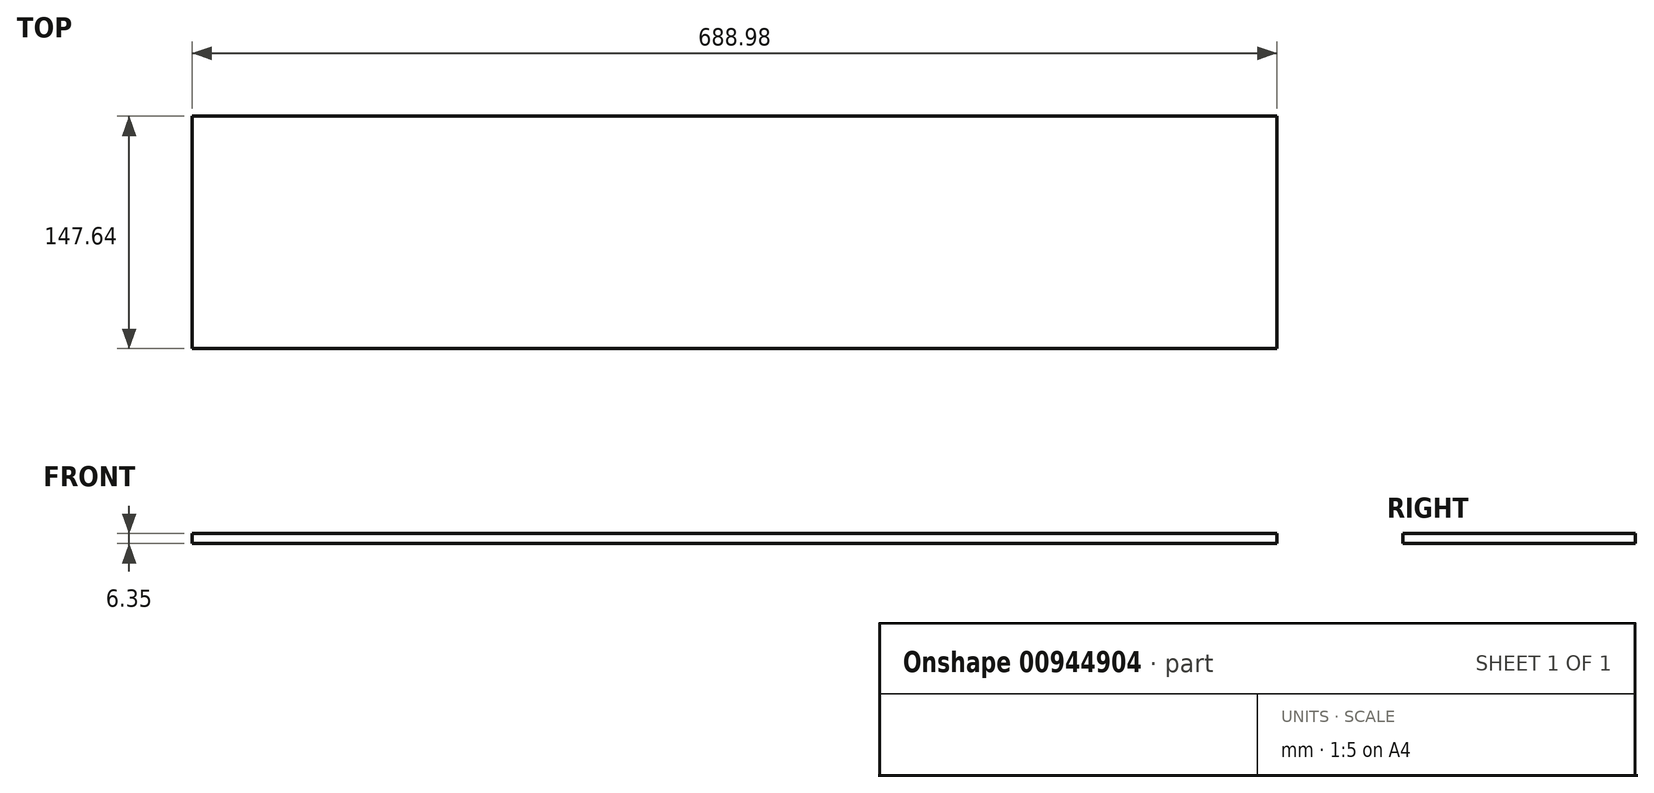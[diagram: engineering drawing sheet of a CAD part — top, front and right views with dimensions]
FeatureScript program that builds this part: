
annotation { "Feature Type Name" : "Feature", "Feature Type Description" : "" }
export const myFeature = defineFeature(function(context is Context, id is Id, definition is map)
    precondition{}
    {
        {
            var Q0;
            Q0=qCreatedBy(makeId("Top.planeOp"),FACE);
            var sketch = newSketch(context, id + "F0", { "sketchPlane" : qUnion([Q0])});
            skLineSegment(sketch, "E0.bottom", {"start": v(-953.72, 1555.2) * mm, "end": v(30.53, 1555.2) * mm});
            skLineSegment(sketch, "E0.top", {"start": v(-953.72, -45) * mm, "end": v(30.53, -45) * mm});
            skLineSegment(sketch, "E0.left", {"start": v(-953.72, 1555.2) * mm, "end": v(-953.72, -45) * mm});
            skLineSegment(sketch, "E0.right", {"start": v(30.53, 1555.2) * mm, "end": v(30.53, -45) * mm});
            skLineSegment(sketch, "E1", {"start": v(-806.08, 1555.2) * mm, "end": v(-806.08, -45) * mm});
            skLineSegment(sketch, "E2", {"start": v(-953.72, 1555.2) * mm, "end": v(-806.08, 1555.2) * mm});
            skLineSegment(sketch, "E3.0", {"start": v(-802.9, 1555.2) * mm, "end": v(-802.9, -45) * mm});
            skLineSegment(sketch, "E4", {"start": v(30.53, 1555.2) * mm, "end": v(-117.1, 1555.2) * mm});
            skLineSegment(sketch, "E5", {"start": v(-117.1, 1555.2) * mm, "end": v(-117.1, -45) * mm});
            skLineSegment(sketch, "E6.0", {"start": v(-120.28, 1555.2) * mm, "end": v(-120.28, -45) * mm});
            skLineSegment(sketch, "E7", {"start": v(-953.72, 1555.2) * mm, "end": v(-953.72, 1407.57) * mm});
            skLineSegment(sketch, "E8", {"start": v(-953.72, 1407.57) * mm, "end": v(30.53, 1407.57) * mm});
            skLineSegment(sketch, "E9.0", {"start": v(-953.72, 1404.4) * mm, "end": v(30.53, 1404.4) * mm});
            skLineSegment(sketch, "E10", {"start": v(-953.72, -45) * mm, "end": v(-953.72, 102.65) * mm});
            skLineSegment(sketch, "E11", {"start": v(-953.72, 102.65) * mm, "end": v(30.53, 102.65) * mm});
            skLineSegment(sketch, "E12.0", {"start": v(-953.72, 105.82) * mm, "end": v(30.53, 105.82) * mm});
            skLineSegment(sketch, "E13.bottom", {"start": v(593.6, 1457) * mm, "end": v(1577.84, 1457) * mm});
            skLineSegment(sketch, "E13.top", {"start": v(593.6, -143.2) * mm, "end": v(1577.84, -143.2) * mm});
            skLineSegment(sketch, "E13.left", {"start": v(593.6, 1457) * mm, "end": v(593.6, -143.2) * mm});
            skLineSegment(sketch, "E13.right", {"start": v(1577.84, 1457) * mm, "end": v(1577.84, -143.2) * mm});
            skLineSegment(sketch, "E14", {"start": v(728.53, 1457) * mm, "end": v(728.53, -143.2) * mm});
            skLineSegment(sketch, "E15", {"start": v(593.6, 1457) * mm, "end": v(728.53, 1457) * mm});
            skLineSegment(sketch, "E16.0", {"start": v(731.7, 1457) * mm, "end": v(731.7, -143.2) * mm});
            skLineSegment(sketch, "E17", {"start": v(1577.84, 1457) * mm, "end": v(1430.2, 1457) * mm});
            skLineSegment(sketch, "E18", {"start": v(1430.2, 1457) * mm, "end": v(1430.2, -143.2) * mm});
            skLineSegment(sketch, "E19.0", {"start": v(1427.03, 1457) * mm, "end": v(1427.03, -143.2) * mm});
            skLineSegment(sketch, "E20", {"start": v(593.6, 1322.06) * mm, "end": v(1577.84, 1322.06) * mm});
            skLineSegment(sketch, "E21.0", {"start": v(593.6, 1318.88) * mm, "end": v(1577.84, 1318.88) * mm});
            skLineSegment(sketch, "E22", {"start": v(593.6, -143.2) * mm, "end": v(593.6, 4.43) * mm});
            skLineSegment(sketch, "E23", {"start": v(593.6, 4.43) * mm, "end": v(1577.84, 4.43) * mm});
            skLineSegment(sketch, "E24.0", {"start": v(593.6, 7.6) * mm, "end": v(1577.84, 7.6) * mm});
            skLineSegment(sketch, "E25", {"start": v(593.6, 1457) * mm, "end": v(593.6, 1322.06) * mm});
            skLineSegment(sketch, "E26", {"start": v(1577.84, 4.43) * mm, "end": v(1577.84, -143.2) * mm});
            skLineSegment(sketch, "E27", {"start": v(1577.84, -143.2) * mm, "end": v(1430.2, -143.2) * mm});
            skSolve(sketch);
        }
        {
            var Q0;
            {var subQ0=sQuery(id+"F0.wireOp",EDGE,"E3.0");var subQ1=sQuery(id+"F0.wireOp",EDGE,"E0.bottom");var subQ2=makeQuery(id+"F0.imprint","INTERSECT",VERTEX,{"derivedFrom":[subQ1,subQ0]});var subQ10=sQuery(id+"F0.wireOp",EDGE,"E5");var subQ11=makeQuery(id+"F0.imprint","INTERSECT",VERTEX,{"derivedFrom":[subQ1,subQ10]});Q0=qUnion([makeQuery(id+"F0.imprint","IMPRINT",FACE,{"disambiguationData":[TD([[makeQuery(id+"F0.imprint","IMPRINT",EDGE,{"disambiguationData":[TD([[subQ2,1.0]])],"derivedFrom":subQ1}),-1.0]])]}),makeQuery(id+"F0.imprint","IMPRINT",FACE,{"disambiguationData":[TD([[makeQuery(id+"F0.imprint","IMPRINT",EDGE,{"disambiguationData":[TD([[subQ11,1.0]])],"derivedFrom":subQ1}),-1.0]])]}),makeQuery(id+"F0.imprint","IMPRINT",FACE,{"disambiguationData":[TD([[makeQuery(id+"F0.imprint","IMPRINT",EDGE,{"disambiguationData":[TD([[subQ2,-1.0]])],"derivedFrom":subQ1}),-1.0]])]})]);}
            extrude(context, id + "F1", {"entities" : qUnion([Q0]), "depth" : 6.35 * mm, "offsetDistance" : 25.4 * mm});
        }
    });
